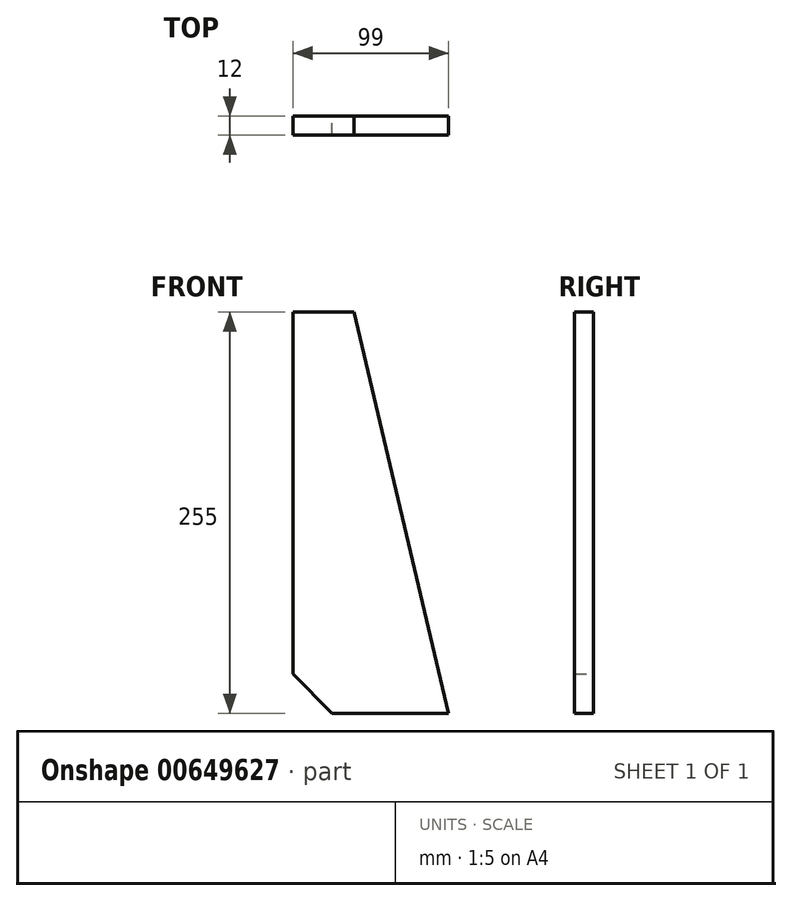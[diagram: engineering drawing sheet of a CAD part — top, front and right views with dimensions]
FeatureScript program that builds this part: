
annotation { "Feature Type Name" : "Feature", "Feature Type Description" : "" }
export const myFeature = defineFeature(function(context is Context, id is Id, definition is map)
    precondition{}
    {
        {
            var Q0;
            Q0=qCreatedBy(makeId("Front.planeOp"),FACE);
            var sketch = newSketch(context, id + "F0", { "sketchPlane" : qUnion([Q0])});
            skLineSegment(sketch, "E0.bottom", {"start": v(49.5, -127.5) * mm, "end": v(-49.5, -127.5) * mm});
            skLineSegment(sketch, "E0.top", {"start": v(49.5, 127.5) * mm, "end": v(-49.5, 127.5) * mm});
            skLineSegment(sketch, "E0.left", {"start": v(49.5, -127.5) * mm, "end": v(49.5, 127.5) * mm});
            skLineSegment(sketch, "E0.right", {"start": v(-49.5, -127.5) * mm, "end": v(-49.5, 127.5) * mm});
            skPoint(sketch, "E0.middle", {"position": v(0, 0) * mm});
            skLineSegment(sketch, "E1", {"start": v(-49.5, -102.5) * mm, "end": v(-24.5, -127.5) * mm});
            skLineSegment(sketch, "E2", {"start": v(-24.5, -127.5) * mm, "end": v(-24.5, -127.5) * mm});
            skLineSegment(sketch, "E3", {"start": v(-10.5, 127.5) * mm, "end": v(49.5, -127.5) * mm});
            skSolve(sketch);
        }
        {
            var Q0;
            {var subQ0=sQuery(id+"F0.wireOp",EDGE,"E1");Q0=makeQuery(id+"F0.imprint","IMPRINT",FACE,{"disambiguationData":[TD([[makeQuery(id+"F0.imprint","IMPRINT",EDGE,{"derivedFrom":subQ0}),1.0]])]});}
            extrude(context, id + "F1", {"entities" : qUnion([Q0]), "depth" : 12 * mm, "offsetDistance" : 25 * mm, "symmetric" : true});
        }
    });
